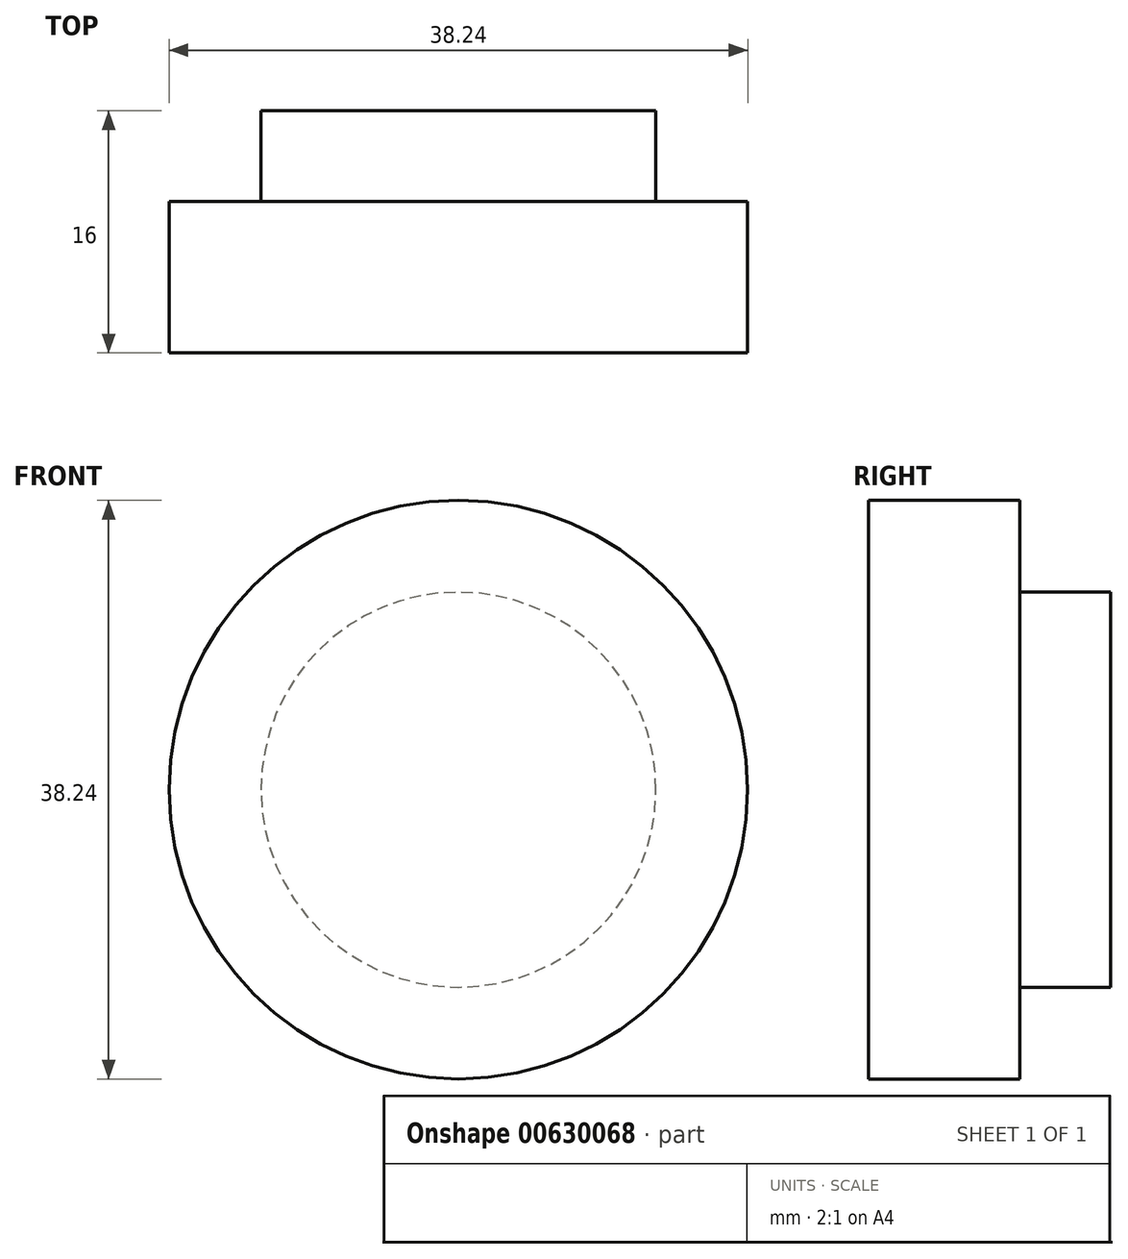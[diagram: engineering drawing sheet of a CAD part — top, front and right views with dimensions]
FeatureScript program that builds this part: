
annotation { "Feature Type Name" : "Feature", "Feature Type Description" : "" }
export const myFeature = defineFeature(function(context is Context, id is Id, definition is map)
    precondition{}
    {
        {
            var Q0;
            Q0=qCreatedBy(makeId("Front.planeOp"),FACE);
            var sketch = newSketch(context, id + "F0", { "sketchPlane" : qUnion([Q0])});
            skCircle(sketch, "E0", {"center": v(0, 0) * mm, "radius": 19.12 * mm});
            skSolve(sketch);
        }
        {
            var Q0;
            Q0 = qSketchRegion(id + "F0", true);
            extrude(context, id + "F1", {"entities" : qUnion([Q0]), "depth" : 10 * mm, "offsetDistance" : 25 * mm});
        }
        {
            var Q0;
            Q0=makeQuery(id+"F1.opExtrude","CAP_FACE",FACE,{"disambiguationData":[OSD([sQuery(id+"F0.wireOp",EDGE,"E0")])],"isStart":false});
            var sketch = newSketch(context, id + "F2", { "sketchPlane" : qUnion([Q0])});
            skCircle(sketch, "E1", {"center": v(0, 0) * mm, "radius": 13.05 * mm});
            skSolve(sketch);
        }
        {
            var Q0;
            Q0 = qSketchRegion(id + "F2", true);
            extrude(context, id + "F3", {"entities" : qUnion([Q0]), "operationType" : NewBodyOperationType.ADD, "oppositeDirection" : true, "depth" : 16 * mm, "offsetDistance" : 25 * mm});
        }
    });
